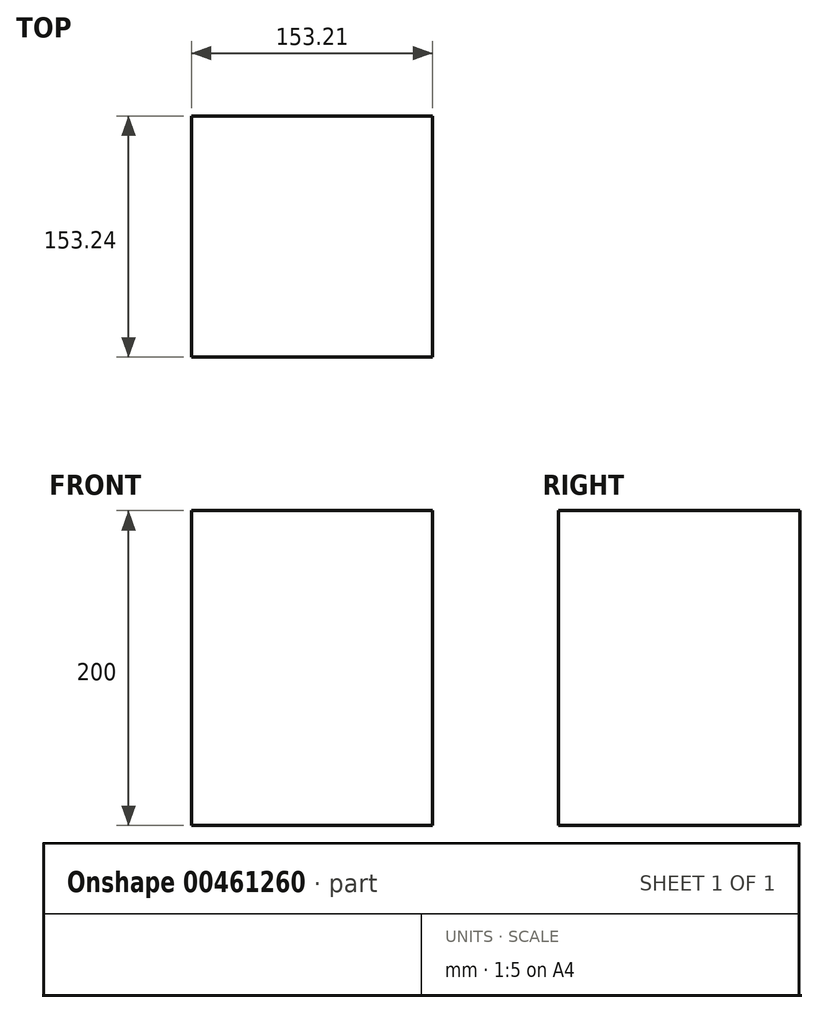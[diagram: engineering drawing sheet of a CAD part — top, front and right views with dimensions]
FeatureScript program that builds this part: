
annotation { "Feature Type Name" : "Feature", "Feature Type Description" : "" }
export const myFeature = defineFeature(function(context is Context, id is Id, definition is map)
    precondition{}
    {
        {
            var Q0;
            Q0=qCreatedBy(makeId("Top.planeOp"),FACE);
            var sketch = newSketch(context, id + "F0", { "sketchPlane" : qUnion([Q0])});
            skLineSegment(sketch, "E0.bottom", {"start": v(-76.93, 77.18) * mm, "end": v(76.28, 77.18) * mm});
            skLineSegment(sketch, "E0.top", {"start": v(-76.93, -76.06) * mm, "end": v(76.28, -76.06) * mm});
            skLineSegment(sketch, "E0.left", {"start": v(-76.93, 77.18) * mm, "end": v(-76.93, -76.06) * mm});
            skLineSegment(sketch, "E0.right", {"start": v(76.28, 77.18) * mm, "end": v(76.28, -76.06) * mm});
            skSolve(sketch);
        }
        {
            var Q0;
            Q0 = qSketchRegion(id + "F0", true);
            extrude(context, id + "F1", {"entities" : qUnion([Q0]), "depth" : 200 * mm, "offsetDistance" : 25.4 * mm});
        }
    });
